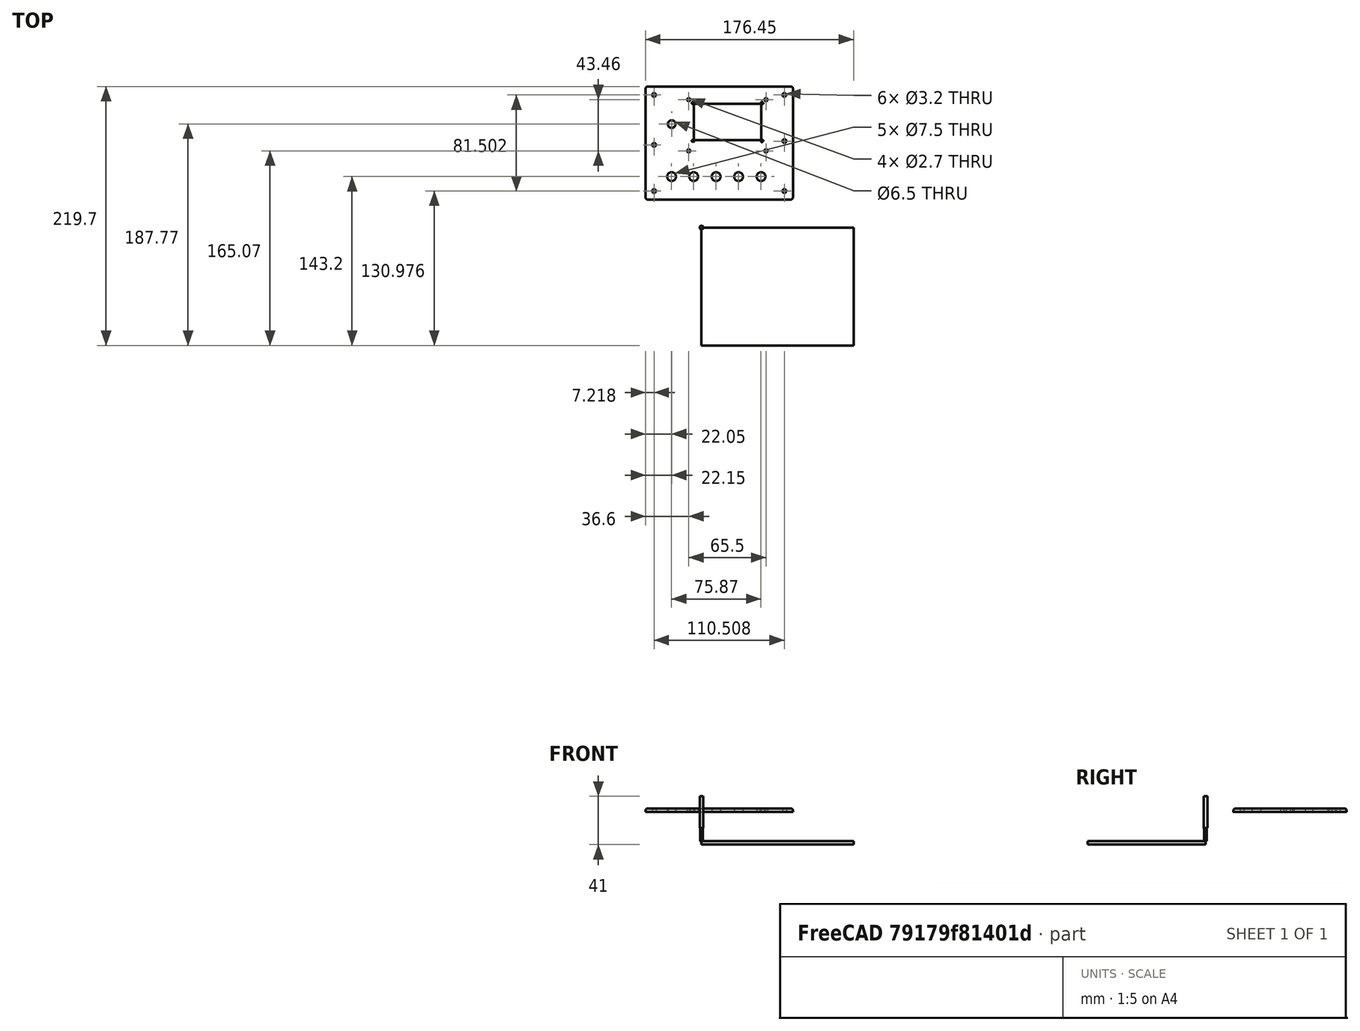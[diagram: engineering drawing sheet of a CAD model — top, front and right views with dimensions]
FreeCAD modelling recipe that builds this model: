
FCSTD DOCUMENT  (FreeCAD 0.21R33771 (Git))
Label: Top Plate CNC Job
License: All rights reserved
LicenseURL: http://en.wikipedia.org/wiki/All_rights_reserved
objects: Path::FeaturePython×4, Part::FeaturePython×3, App::DocumentObjectGroup×3, Part::Feature×1, App::Part×1, App::FeaturePython×1
note: 6 computed .brp shape members not serialized (recipe doc carries the construction recipe); baked Part::Feature solids carry a one-line shape summary decoded from their .brp

FEATURE [Part::Feature] Part__Feature  label="Top Plate"
  Placement = pos=(0,0,24.7) rot=(0,0,1;0rad)
  shape: bbox 125 x 96 x 3 mm, 50 faces (baked)
FEATURE [App::Part] Top_Enclosure_Plate  label="Top Enclosure Plate"
  Group = -> [Part__Feature]
  Origin = -> Origin
FEATURE [App::FeaturePython] SetupSheet  # Path/CAM operation (typed FeaturePython)
  ClearanceHeightExpression = OpStockZMax+SetupSheet.ClearanceHeightOffset
  ClearanceHeightOffset = 5
  CoolantMode = 0
  CoolantModes = None | Flood | Mist
  FinalDepthExpression = OpFinalDepth
  HorizRapid = 0
  SafeHeightExpression = OpStockZMax+SetupSheet.SafeHeightOffset
  SafeHeightOffset = 3
  StartDepthExpression = OpStartDepth
  StepDownExpression = OpToolDiameter
  VertRapid = 0
FEATURE [Part::FeaturePython] Clone  label="Model-Top Enclosure Plate"  # Draft clone (typed FeaturePython)
  AttacherType = Attacher::AttachEngine3D
  Fuse = false
  Objects = -> [Top_Enclosure_Plate]
  PathResource = Model
  Placement = pos=(49.4504,-121.7,-27.7) rot=(0,0,1;0rad)
  Scale = (1,1,1)
FEATURE [App::DocumentObjectGroup] Model
  Group = -> [Clone]
FEATURE [Part::FeaturePython] ToolBit  label="Endmill"  # Path/CAM toolbit (typed FeaturePython)
  BitPropertyNames = Chipload | CuttingEdgeHeight | Diameter | Flutes | Length | Material | ShankDiameter | SpindleDirection
  BitShape = C:/Program Files/FreeCAD 0.21/Mod\Path\Tools\Shape\endmill.fcstd
  Chipload = 0
  CuttingEdgeHeight = 11
  Diameter = 2.3
  Flutes = 0
  Length = 38
  Material = 0
  ShankDiameter = 3.1
  ShapeName = endmill
  SpindleDirection = 0
FEATURE [Path::FeaturePython] TC__Default_Tool  label="TC: EndMill01"  # Path/CAM operation (typed FeaturePython)
  HorizFeed = 3.33333
  HorizRapid = 0
  SpindleDir = 0
  SpindleSpeed = 10000
  Tool = -> ToolBit
  ToolNumber = 10
  VertFeed = 2
  VertRapid = 0
  expr: HorizRapid = SetupSheet.HorizRapid
  expr: VertRapid = SetupSheet.VertRapid
FEATURE [App::DocumentObjectGroup] Tools
  Group = -> [TC__Default_Tool]
FEATURE [Part::FeaturePython] Stock001  # WARN: FeaturePython — macro-defined, semantics opaque (R4)
  Height = 3
  Length = 129
  Placement = pos=(0,-100,-3) rot=(0,0,1;0rad)
  StockType = CreateBox
  Width = 100
FEATURE [Path::FeaturePython] Pocket_Shape001  label="Display Pocket"  # Path/CAM operation (typed FeaturePython)
  Active = true
  AreaParams:
    Tolerance = 1e-07
    FitArcs = True
    Simplify = False
    CleanDistance = 0.0
    Accuracy = 0.01
    Unit = 1.0
    MinArcPoints = 4
    MaxArcPoints = 100
    ClipperScale = 10000000.0
    Fill = 0
    Coplanar = 0
    Reorient = True
    Outline = False
    Explode = False
    OpenMode = 0
    Deflection = 0.01
    SubjectFill = 0
    ClipFill = 0
    Offset = 0.0
    ExtraPass = 0
    Stepover = 0.0
    LastStepover = 0.0
    JoinType = 0
    EndType = 0
    MiterLimit = 2.0
    RoundPrecision = 0.0
    PocketMode = 2
    ToolRadius = 1.15
    PocketExtraOffset = 0.0
    PocketStepover = 1.15
    PocketLastStepover = 0.0
    FromCenter = True
    Angle = 45.0
    AngleShift = 0.0
    Shift = 0.0
    Thicken = False
    SectionCount = -1
    Stepdown = 1.0
    SectionOffset = 0.0
    SectionTolerance = 1e-07
    SectionMode = 2
    Project = False
  Base = -> [Clone]
  ClearanceHeight = 5
  CoolantMode = 0
  CutMode = 0
  CycleTime = 00:18:20
  ExtensionCorners = true
  ExtensionLengthDefault = 1.15
  ExtraOffset = 0
  FinalDepth = -3
  FinishDepth = 0
  KeepToolDown = false
  MinTravel = false
  OffsetPattern = 1
  OpFinalDepth = -3
  OpStartDepth = 0
  OpStockZMax = 0
  OpStockZMin = -3
  OpToolDiameter = 2.3
  PathParams = {'orientation': 1, 'feedrate': 3.3333333333333335, 'feedrate_v': 2.0, 'verbose': True, 'resume_height': 3.0, 'retraction': 5.0, 'return_end': True, 'preamble': False}
  PocketLastStepOver = 0
  SafeHeight = 3
  SplitArcs = false
  StartAt = 0
  StartDepth = 0
  StartPoint = (0,0,0)
  StepDown = 2.3
  StepOver = 50
  ToolController = -> TC__Default_Tool
  UseOutline = false
  UseStartPoint = false
  ZigZagAngle = 45
  expr: ClearanceHeight = OpStockZMax + SetupSheet.ClearanceHeightOffset
  expr: ExtensionLengthDefault = OpToolDiameter / 2
  expr: FinalDepth = OpFinalDepth
  expr: SafeHeight = OpStockZMax + SetupSheet.SafeHeightOffset
  expr: StartDepth = OpStartDepth
  expr: StepDown = OpToolDiameter
FEATURE [Path::FeaturePython] Profile  # Path/CAM operation (typed FeaturePython)
  Active = true
  AreaParams:
    Tolerance = 1e-07
    FitArcs = True
    Simplify = False
    CleanDistance = 0.0
    Accuracy = 0.01
    Unit = 1.0
    MinArcPoints = 4
    MaxArcPoints = 100
    ClipperScale = 10000000.0
    Fill = 0
    Coplanar = 0
    Reorient = True
    Outline = False
    Explode = False
    OpenMode = 0
    Deflection = 0.01
    SubjectFill = 0
    ClipFill = 0
    Offset = 1.15
    ExtraPass = 0
    Stepover = 0.0
    LastStepover = 0.0
    JoinType = 0
    EndType = 0
    MiterLimit = 2.0
    RoundPrecision = 0.0
    PocketMode = 0
    ToolRadius = 1.0
    PocketExtraOffset = 0.0
    PocketStepover = 0.0
    PocketLastStepover = 0.0
    FromCenter = False
    Angle = 45.0
    AngleShift = 0.0
    Shift = 0.0
    Thicken = False
    SectionCount = -1
    Stepdown = 1.0
    SectionOffset = 0.0
    SectionTolerance = 1e-07
    SectionMode = 2
    Project = False
  Base = -> [Clone]
  ClearanceHeight = 5
  CoolantMode = 0
  CycleTime = 00:05:13
  Direction = 0
  FinalDepth = -3
  HandleMultipleFeatures = 0
  JoinType = 0
  MiterLimit = 0.1
  OffsetExtra = 0
  OpFinalDepth = -3
  OpStartDepth = 0
  OpStockZMax = 0
  OpStockZMin = -3
  OpToolDiameter = 2.3
  PathParams = {'orientation': 1, 'feedrate': 3.3333333333333335, 'feedrate_v': 2.0, 'verbose': True, 'resume_height': 3.0, 'retraction': 5.0, 'return_end': True, 'preamble': False}
  SafeHeight = 3
  Side = 0
  SplitArcs = false
  StartDepth = 0
  StartPoint = (0,0,0)
  StepDown = 2.3
  ToolController = -> TC__Default_Tool
  UseComp = true
  UseStartPoint = false
  processCircles = false
  processHoles = false
  processPerimeter = true
  expr: ClearanceHeight = OpStockZMax + SetupSheet.ClearanceHeightOffset
  expr: FinalDepth = OpFinalDepth
  expr: SafeHeight = OpStockZMax + SetupSheet.SafeHeightOffset
  expr: StartDepth = OpStartDepth
  expr: StepDown = OpToolDiameter
FEATURE [Path::FeaturePython] Helix  # Path/CAM operation (typed FeaturePython)
  Active = true
  Base = -> [Clone]
  ClearanceHeight = 5
  CoolantMode = 0
  CycleTime = 00:07:25
  Direction = 0
  FinalDepth = -3
  OffsetExtra = 0
  OpFinalDepth = -3
  OpStartDepth = 0
  OpStockZMax = 0
  OpStockZMin = -3
  OpToolDiameter = 2.3
  SafeHeight = 3
  StartDepth = 0
  StartRadius = 0
  StartSide = 0
  StepDown = 2.3
  StepOver = 50
  ToolController = -> TC__Default_Tool
  expr: ClearanceHeight = OpStockZMax + SetupSheet.ClearanceHeightOffset
  expr: FinalDepth = OpFinalDepth
  expr: SafeHeight = OpStockZMax + SetupSheet.SafeHeightOffset
  expr: StartDepth = OpStartDepth
  expr: StepDown = OpToolDiameter
FEATURE [App::DocumentObjectGroup] Operations
  Group = -> [Pocket_Shape001,Helix,Profile]
